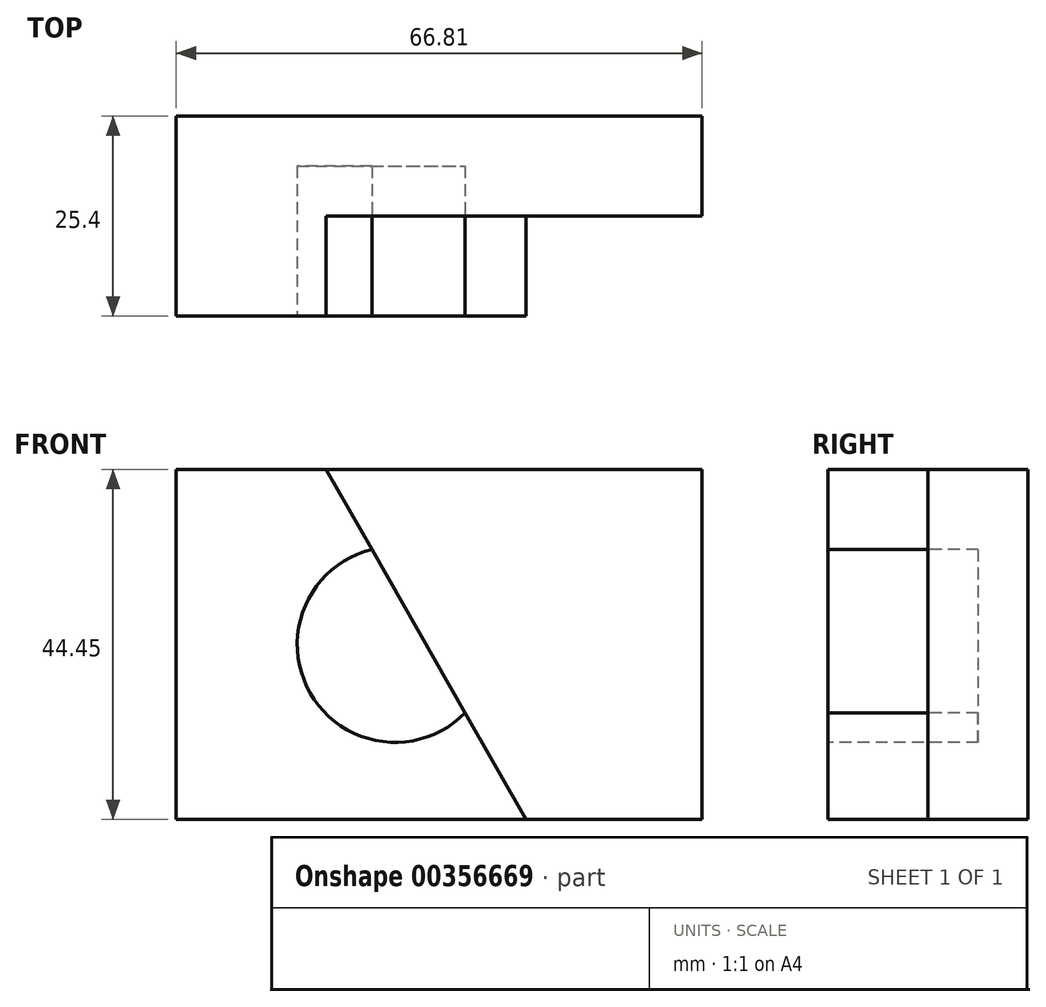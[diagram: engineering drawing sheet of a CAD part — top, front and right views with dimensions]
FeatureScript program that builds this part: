
annotation { "Feature Type Name" : "Feature", "Feature Type Description" : "" }
export const myFeature = defineFeature(function(context is Context, id is Id, definition is map)
    precondition{}
    {
        {
            var Q0;
            Q0=qCreatedBy(makeId("Front.planeOp"),FACE);
            var sketch = newSketch(context, id + "F0", { "sketchPlane" : qUnion([Q0])});
            skLineSegment(sketch, "E0.bottom", {"start": v(-40.35, 35.5) * mm, "end": v(26.46, 35.5) * mm});
            skLineSegment(sketch, "E0.top", {"start": v(-40.35, -8.94) * mm, "end": v(26.46, -8.94) * mm});
            skLineSegment(sketch, "E0.left", {"start": v(-40.35, 35.5) * mm, "end": v(-40.35, -8.94) * mm});
            skLineSegment(sketch, "E0.right", {"start": v(26.46, 35.5) * mm, "end": v(26.46, -8.94) * mm});
            skSolve(sketch);
        }
        {
            var Q0;
            Q0=makeQuery(id+"F0.imprint","IMPRINT",FACE,{"disambiguationData":[TD([[makeQuery(id+"F0.imprint","IMPRINT",EDGE,{"derivedFrom":sQuery(id+"F0.wireOp",EDGE,"E0.bottom")}),-1.0]])]});
            extrude(context, id + "F1", {"entities" : qUnion([Q0]), "depth" : 25.4 * mm});
        }
        {
            var Q0;
            Q0=makeQuery(id+"F1.opExtrude","CAP_FACE",FACE,{"disambiguationData":[OSD([sQuery(id+"F0.wireOp",EDGE,"E0.bottom"),sQuery(id+"F0.wireOp",EDGE,"E0.top"),sQuery(id+"F0.wireOp",EDGE,"E0.left"),sQuery(id+"F0.wireOp",EDGE,"E0.right")])],"isStart":false});
            var sketch = newSketch(context, id + "F2", { "sketchPlane" : qUnion([Q0])});
            skLineSegment(sketch, "E1", {"start": v(-40.35, 35.5) * mm, "end": v(-21.3, 35.5) * mm});
            skLineSegment(sketch, "E2", {"start": v(-21.3, 35.5) * mm, "end": v(4.1, -8.94) * mm});
            skLineSegment(sketch, "E3", {"start": v(4.1, -8.94) * mm, "end": v(-40.35, -8.94) * mm});
            skLineSegment(sketch, "E4", {"start": v(-40.35, -8.94) * mm, "end": v(-40.35, 35.5) * mm});
            skSolve(sketch);
        }
        {
            var Q0;
            {var subQ0=sQuery(id+"F2.wireOp",EDGE,"E2");Q0=makeQuery(id+"F2.imprint","IMPRINT",FACE,{"disambiguationData":[TD([[makeQuery(id+"F2.imprint","IMPRINT",EDGE,{"derivedFrom":subQ0}),1.0]])]});}
            extrude(context, id + "F3", {"entities" : qUnion([Q0]), "operationType" : NewBodyOperationType.REMOVE, "oppositeDirection" : true, "depth" : 12.7 * mm});
        }
        {
            var Q0;
            Q0=makeQuery(id+"F1.opExtrude","CAP_FACE",FACE,{"disambiguationData":[OSD([sQuery(id+"F0.wireOp",EDGE,"E0.bottom"),sQuery(id+"F0.wireOp",EDGE,"E0.top"),sQuery(id+"F0.wireOp",EDGE,"E0.left"),sQuery(id+"F0.wireOp",EDGE,"E0.right")])],"isStart":false});
            var sketch = newSketch(context, id + "F4", { "sketchPlane" : qUnion([Q0])});
            skCircle(sketch, "E5", {"center": v(-12.53, 13.28) * mm, "radius": 12.43 * mm});
            skPoint(sketch, "E5.centerSnap0", {"position": v(-8.6, 13.28) * mm});
            skSolve(sketch);
        }
        {
            var Q0;
            {var subQ0=sQuery(id+"F4.wireOp",EDGE,"E5");var subQ1=makeQuery(id+"F3.boolean.opBoolean","COPY",EDGE,{"derivedFrom":makeQuery(id+"F3.opExtrude","CAP_EDGE",EDGE,{"disambiguationData":[OSD([sQuery(id+"F2.wireOp",EDGE,"E2")])],"isStart":true})});var subQ2=makeQuery(id+"F4.imprint","INTERSECT",VERTEX,{"disambiguationData":[OD(0.0)],"derivedFrom":[subQ1,subQ0]});Q0=makeQuery(id+"F4.imprint","IMPRINT",FACE,{"disambiguationData":[TD([[makeQuery(id+"F4.imprint","IMPRINT",EDGE,{"disambiguationData":[TD([[subQ2,-1.0]])],"derivedFrom":subQ0}),1.0]])]});}
            extrude(context, id + "F5", {"entities" : qUnion([Q0]), "operationType" : NewBodyOperationType.REMOVE, "oppositeDirection" : true, "depth" : 19.05 * mm});
        }
    });
